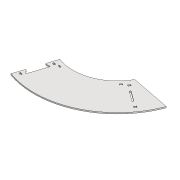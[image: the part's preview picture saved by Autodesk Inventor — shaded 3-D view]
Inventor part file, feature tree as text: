
AUTODESK INVENTOR PART (.ipt)
format: ipt  version: 2020 (Build 240168000, 168)  size: 316,928 bytes
history: native  units: mm
features: extrude x1, sketch x1
ambient origin geometry x8: Origin, YZ Plane, XZ Plane, XY Plane, X Axis, Y Axis, Z Axis, Center Point
bodies: Solid1 (feature_tree)
feature tree (2):
  extrude  "Extrusion1"  Depth=1.75mm
  sketch  "Sketch1"  dims[d0=504.787567mm d1=944.787567mm d2=50.0mm d4=360.0deg d6=7.5mm d7=7.5mm d9=68.5mm d10=7.5mm d11=7.5mm d12=3.5mm d13=3.5mm d17=50.0mm d19=360.0deg d21=4.363323mm d25=10.0mm d26=10.0mm d27=1.75mm d28=30.0mm d30=25.132741mm d32=271.25mm d33=7.5mm d34=13.5mm d36=1.75mm d40=20.0mm d44=7.0mm d45=0.0mm d46=0.0mm d47=8.0mm d48=1.75mm d50=50.0mm d52=50.0mm d54=30.0mm d62=50.0mm d64=50.0mm d66=30.0mm d67=1.75mm]
